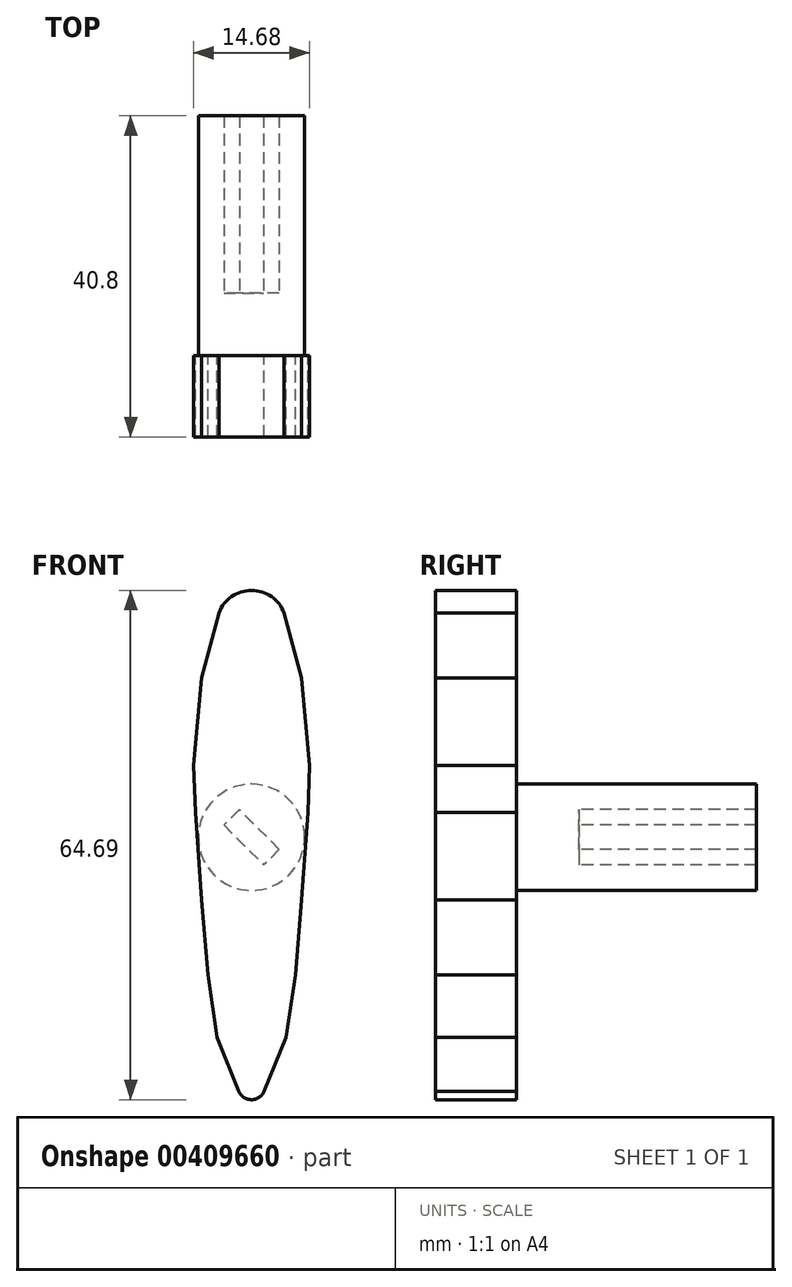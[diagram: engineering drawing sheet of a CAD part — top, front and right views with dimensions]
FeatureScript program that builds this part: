
annotation { "Feature Type Name" : "Feature", "Feature Type Description" : "" }
export const myFeature = defineFeature(function(context is Context, id is Id, definition is map)
    precondition{}
    {
        {
            var Q0;
            Q0=qCreatedBy(makeId("Front.planeOp"),FACE);
            var sketch = newSketch(context, id + "F0", { "sketchPlane" : qUnion([Q0])});
            skLineSegment(sketch, "E0", {"start": v(-7.14, 0) * mm, "end": v(7.14, 0) * mm});
            skLineSegment(sketch, "E1", {"start": v(-0.06, -36.51) * mm, "end": v(0.06, -36.51) * mm});
            skLineSegment(sketch, "E2", {"start": v(-7.14, 0) * mm, "end": v(-6.35, -11.11) * mm});
            skLineSegment(sketch, "E3", {"start": v(-6.35, -11.11) * mm, "end": v(-5.56, -20.64) * mm});
            skLineSegment(sketch, "E4", {"start": v(-5.56, -20.64) * mm, "end": v(-4.37, -28.58) * mm});
            skLineSegment(sketch, "E5", {"start": v(-4.37, -28.58) * mm, "end": v(-1.63, -35.41) * mm});
            skLineSegment(sketch, "E6", {"start": v(1.6, -35.48) * mm, "end": v(4.37, -28.58) * mm});
            skLineSegment(sketch, "E7", {"start": v(4.37, -28.58) * mm, "end": v(5.56, -20.64) * mm});
            skLineSegment(sketch, "E8", {"start": v(5.56, -20.64) * mm, "end": v(6.35, -11.11) * mm});
            skLineSegment(sketch, "E9", {"start": v(6.35, -11.11) * mm, "end": v(7.14, 0) * mm});
            skArc(sketch, "E10", {"start": v(-1.63, -35.41) * mm, "mid": v(-0.04, -36.51) * mm, "end": v(1.6, -35.48) * mm});
            skPoint(sketch, "E11.orphan", {"position": v(-1.2, -36.51) * mm});
            skPoint(sketch, "E12.orphan", {"position": v(1.2, -36.51) * mm});
            skLineSegment(sketch, "E13", {"start": v(-0.23, 28.18) * mm, "end": v(0.23, 28.18) * mm});
            skLineSegment(sketch, "E14", {"start": v(-7.14, 0) * mm, "end": v(-7.34, 5.95) * mm});
            skLineSegment(sketch, "E15", {"start": v(-7.34, 5.95) * mm, "end": v(-6.35, 17.07) * mm});
            skLineSegment(sketch, "E16", {"start": v(7.14, 0) * mm, "end": v(7.34, 5.95) * mm});
            skLineSegment(sketch, "E17", {"start": v(7.34, 5.95) * mm, "end": v(6.35, 17.07) * mm});
            skLineSegment(sketch, "E18", {"start": v(-6.35, 17.07) * mm, "end": v(-4.13, 25.34) * mm});
            skLineSegment(sketch, "E19", {"start": v(6.35, 17.07) * mm, "end": v(4.13, 25.34) * mm});
            skArc(sketch, "E20", {"start": v(4.13, 25.34) * mm, "mid": v(0, 28.18) * mm, "end": v(-4.13, 25.34) * mm});
            skSolve(sketch);
        }
        {
            var Q0;
            Q0=qCreatedBy(makeId("Front.planeOp"),FACE);
            var sketch = newSketch(context, id + "F1", { "sketchPlane" : qUnion([Q0])});
            skCircle(sketch, "E21", {"center": v(0, -3.18) * mm, "radius": 6.75 * mm});
            skSolve(sketch);
        }
        {
            var Q0;
            Q0=qCreatedBy(makeId("Front.planeOp"),FACE);
            var sketch = newSketch(context, id + "F2", { "sketchPlane" : qUnion([Q0])});
            skLineSegment(sketch, "E22", {"start": v(-2.53, -0.65) * mm, "end": v(-1.54, 0.33) * mm});
            skLineSegment(sketch, "E23.MirrorCS", {"start": v(-2.53, -0.65) * mm, "end": v(-3.5, -1.63) * mm});
            skLineSegment(sketch, "E24.MirrorCS", {"start": v(2.53, -5.7) * mm, "end": v(3.5, -4.72) * mm});
            skLineSegment(sketch, "E25.MirrorCS", {"start": v(2.53, -5.7) * mm, "end": v(1.54, -6.68) * mm});
            skLineSegment(sketch, "E26", {"start": v(-3.5, -1.63) * mm, "end": v(1.54, -6.68) * mm});
            skLineSegment(sketch, "E27", {"start": v(3.5, -4.72) * mm, "end": v(-1.54, 0.33) * mm});
            skPoint(sketch, "E28.end.orphan", {"position": v(-3.65, 0.47) * mm});
            skSolve(sketch);
        }
        {
            var Q0;
            Q0=qCreatedBy(makeId("Front.planeOp"),FACE);
            var sketch = newSketch(context, id + "F3", { "sketchPlane" : qUnion([Q0])});
            skLineSegment(sketch, "E29", {"start": v(-2.53, -0.65) * mm, "end": v(-1.54, 0.33) * mm});
            skLineSegment(sketch, "E30.MirrorCS", {"start": v(-2.53, -0.65) * mm, "end": v(-3.5, -1.63) * mm});
            skLineSegment(sketch, "E31.MirrorCS", {"start": v(2.53, -5.7) * mm, "end": v(3.5, -4.72) * mm});
            skLineSegment(sketch, "E32.MirrorCS", {"start": v(2.53, -5.7) * mm, "end": v(1.54, -6.68) * mm});
            skLineSegment(sketch, "E33", {"start": v(-3.5, -1.63) * mm, "end": v(1.54, -6.68) * mm});
            skLineSegment(sketch, "E34", {"start": v(3.5, -4.72) * mm, "end": v(-1.54, 0.33) * mm});
            skPoint(sketch, "E35.end.orphan", {"position": v(-3.65, 0.47) * mm});
            skSolve(sketch);
        }
        {
            var Q0;
            Q0 = qSketchRegion(id + "F0", true);
            extrude(context, id + "F4", {"entities" : qUnion([Q0]), "depth" : 10.32 * mm});
        }
        {
            var Q0;
            Q0 = qSketchRegion(id + "F1", true);
            extrude(context, id + "F5", {"entities" : qUnion([Q0]), "operationType" : NewBodyOperationType.ADD, "oppositeDirection" : true, "depth" : 30.48 * mm});
        }
        {
            var Q0;
            Q0 = qSketchRegion(id + "F2", true);
            extrude(context, id + "F6", {"entities" : qUnion([Q0]), "operationType" : NewBodyOperationType.REMOVE, "oppositeDirection" : true, "depth" : 35.38 * mm});
        }
        {
            var Q0;
            Q0 = qSketchRegion(id + "F3", true);
            extrude(context, id + "F7", {"entities" : qUnion([Q0]), "operationType" : NewBodyOperationType.ADD, "oppositeDirection" : true, "depth" : 7.94 * mm});
        }
    });
